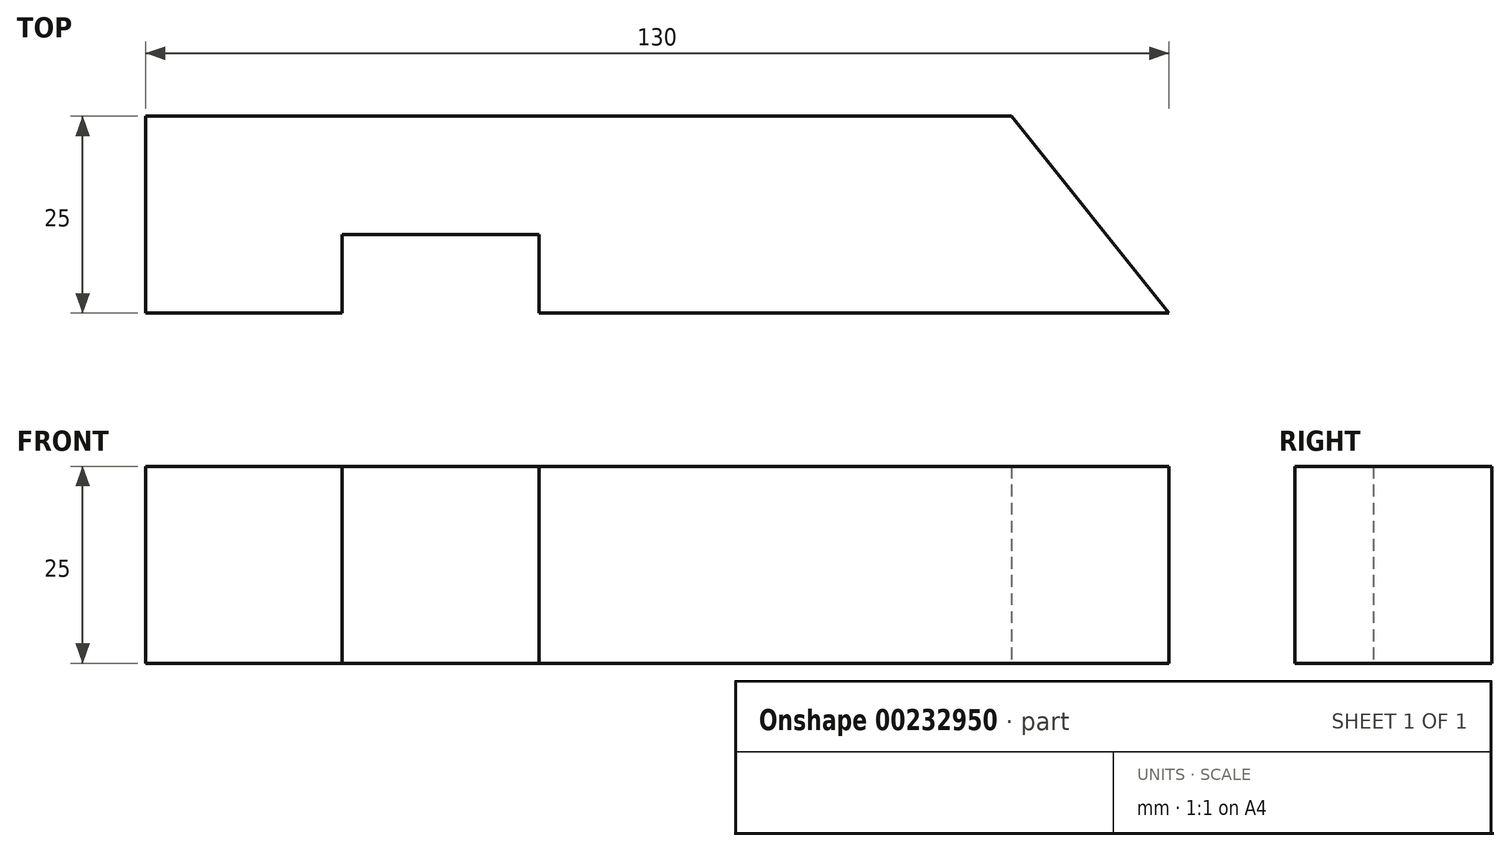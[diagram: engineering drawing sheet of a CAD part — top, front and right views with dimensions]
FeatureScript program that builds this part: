
annotation { "Feature Type Name" : "Feature", "Feature Type Description" : "" }
export const myFeature = defineFeature(function(context is Context, id is Id, definition is map)
    precondition{}
    {
        {
            var Q0;
            Q0=qCreatedBy(makeId("Top.planeOp"),FACE);
            var sketch = newSketch(context, id + "F0", { "sketchPlane" : qUnion([Q0])});
            skLineSegment(sketch, "E0", {"start": v(-91.9, 37.5) * mm, "end": v(18.1, 37.5) * mm});
            skLineSegment(sketch, "E1", {"start": v(-91.9, 37.5) * mm, "end": v(-91.9, 12.5) * mm});
            skLineSegment(sketch, "E2", {"start": v(-91.9, 12.5) * mm, "end": v(-66.9, 12.5) * mm});
            skLineSegment(sketch, "E3", {"start": v(-66.9, 12.5) * mm, "end": v(-66.9, 22.5) * mm});
            skLineSegment(sketch, "E4", {"start": v(-66.9, 22.5) * mm, "end": v(-41.9, 22.5) * mm});
            skLineSegment(sketch, "E5", {"start": v(-41.9, 22.5) * mm, "end": v(-41.9, 12.5) * mm});
            skLineSegment(sketch, "E6", {"start": v(-41.9, 12.5) * mm, "end": v(38.1, 12.5) * mm});
            skLineSegment(sketch, "E7", {"start": v(18.1, 37.5) * mm, "end": v(38.1, 12.5) * mm});
            skSolve(sketch);
        }
        {
            var Q0;
            Q0 = qSketchRegion(id + "F0", true);
            extrude(context, id + "F1", {"entities" : qUnion([Q0]), "depth" : 25 * mm});
        }
    });
